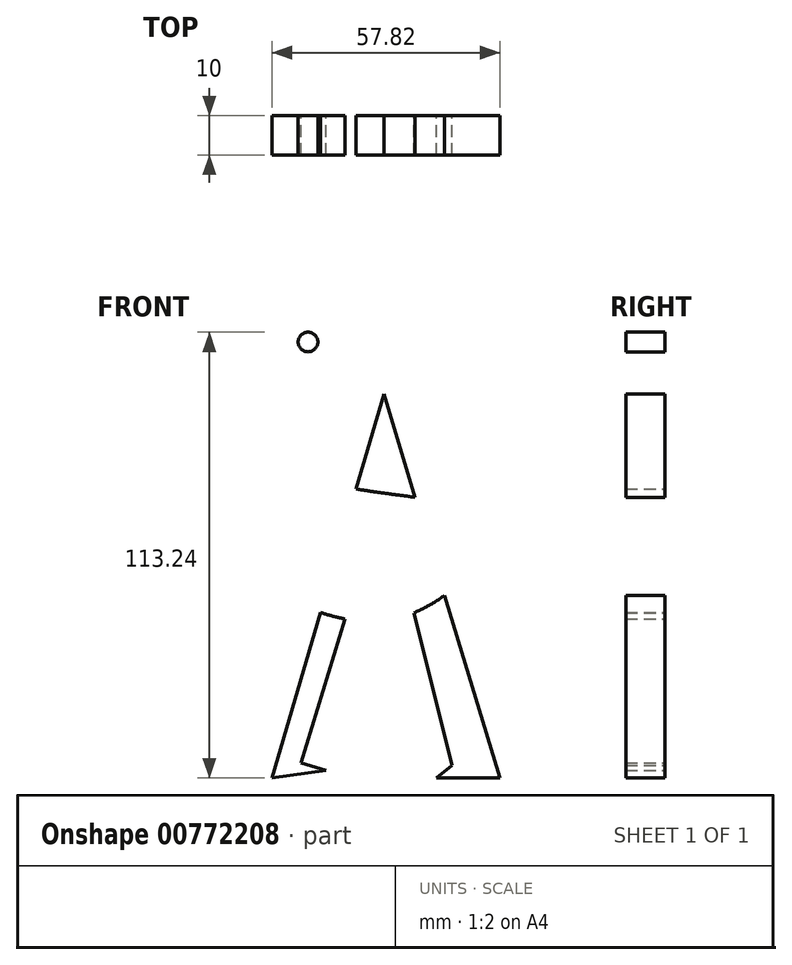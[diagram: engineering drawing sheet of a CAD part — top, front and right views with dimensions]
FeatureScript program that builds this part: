
annotation { "Feature Type Name" : "Feature", "Feature Type Description" : "" }
export const myFeature = defineFeature(function(context is Context, id is Id, definition is map)
    precondition{}
    {
        {
            var Q0;
            Q0=qCreatedBy(makeId("Front.planeOp"),FACE);
            var sketch = newSketch(context, id + "F0", { "sketchPlane" : qUnion([Q0])});
            skFitSpline(sketch, "E0", {"points": [v(-50.96, 0) * mm, v(-14.75, -8.03) * mm, v(8.61, 16.8) * mm, v(-43.07, 32.27) * mm, v(-33.43, 59.72) * mm, v(13.58, 53.58) * mm, v(14.45, 63.51) * mm, v(22.63, 63.51) * mm, v(21.17, 67.6) * mm, v(2.48, 67.02) * mm, v(5.7, 63.8) * mm, v(10.37, 64.1) * mm, v(9.5, 60) * mm, v(-29.35, 67.3) * mm, v(-57.38, 46.28) * mm, v(-41.9, 19.71) * mm, v(-8.03, 16.2) * mm, v(-3.07, 7.15) * mm, v(-24.67, 0) * mm, v(-50.96, 5.4) * mm, v(-63.22, 0) * mm, v(-57.96, -8.61) * mm, v(-61.18, -8.9) * mm, v(-58.55, -12.12) * mm, v(-51.83, -10.37) * mm, v(-53.88, -6.86) * mm, v(-54.75, -6.86) * mm, v(-57.38, -2.2) * mm, v(-50.96, 0) * mm]});
            skLineSegment(sketch, "E1", {"start": v(-45.7, -48.33) * mm, "end": v(-33.5, -6.29) * mm});
            skLineSegment(sketch, "E2", {"start": v(-17.37, 49.2) * mm, "end": v(-9.44, 22.95) * mm});
            skLineSegment(sketch, "E3", {"start": v(12.12, -48.33) * mm, "end": v(-3.94, -48.33) * mm});
            skLineSegment(sketch, "E4", {"start": v(-3.94, -48.33) * mm, "end": v(0, -45.12) * mm});
            skLineSegment(sketch, "E5", {"start": v(0, -45.12) * mm, "end": v(-9.71, -6.4) * mm});
            skLineSegment(sketch, "E6", {"start": v(-17.34, 24) * mm, "end": v(-24.72, 0) * mm});
            skLineSegment(sketch, "E7", {"start": v(-38.4, -44.53) * mm, "end": v(-32.08, -46.47) * mm});
            skLineSegment(sketch, "E8", {"start": v(-32.08, -46.47) * mm, "end": v(-45.7, -48.33) * mm});
            skLineSegment(sketch, "E9.trimOffspring", {"start": v(-27.17, -7.99) * mm, "end": v(-38.4, -44.53) * mm});
            skLineSegment(sketch, "E10.trimOffspring", {"start": v(-11.7, 1.5) * mm, "end": v(-17.34, 24) * mm});
            skLineSegment(sketch, "E11.trimOffspring", {"start": v(-24.38, 25.07) * mm, "end": v(-17.37, 49.2) * mm});
            skLineSegment(sketch, "E12.trimOffspring", {"start": v(-7.3, 15.87) * mm, "end": v(-4.18, 5.57) * mm});
            skLineSegment(sketch, "E13.trimOffspring", {"start": v(-1.9, -1.97) * mm, "end": v(12.12, -48.33) * mm});
            skLineSegment(sketch, "E14.trimOffspring", {"start": v(-31.38, 0.97) * mm, "end": v(-26.58, 17.52) * mm});
            skSolve(sketch);
        }
        {
            var Q0;
            {var subQ0=sQuery(id+"F0.wireOp",EDGE,"E2");Q0=makeQuery(id+"F0.imprint","IMPRINT",FACE,{"disambiguationData":[TD([[makeQuery(id+"F0.imprint","IMPRINT",EDGE,{"derivedFrom":subQ0}),-1.0]])]});}
            var Q1;
            {var subQ0=sQuery(id+"F0.wireOp",EDGE,"E1");Q1=makeQuery(id+"F0.imprint","IMPRINT",FACE,{"disambiguationData":[TD([[makeQuery(id+"F0.imprint","IMPRINT",EDGE,{"derivedFrom":subQ0}),-1.0]])]});}
            var Q2;
            Q2=makeQuery(id+"F0.imprint","IMPRINT",FACE,{"disambiguationData":[TD([[makeQuery(id+"F0.imprint","IMPRINT",EDGE,{"derivedFrom":sQuery(id+"F0.wireOp",EDGE,"E3")}),-1.0]])]});
            extrude(context, id + "F1", {"entities" : qUnion([Q0, Q1, Q2]), "depth" : 10 * mm, "offsetDistance" : 25 * mm});
        }
        {
            var Q0;
            Q0=makeQuery(id+"F1.opExtrude","CAP_FACE",FACE,{"disambiguationData":[OSD([sQuery(id+"F0.wireOp",EDGE,"E0"),sQuery(id+"F0.wireOp",EDGE,"E1"),sQuery(id+"F0.wireOp",EDGE,"E2"),sQuery(id+"F0.wireOp",EDGE,"E3"),sQuery(id+"F0.wireOp",EDGE,"E4"),sQuery(id+"F0.wireOp",EDGE,"E5"),sQuery(id+"F0.wireOp",EDGE,"E6"),sQuery(id+"F0.wireOp",EDGE,"E7"),sQuery(id+"F0.wireOp",EDGE,"E8"),sQuery(id+"F0.wireOp",EDGE,"E9.trimOffspring"),sQuery(id+"F0.wireOp",EDGE,"E10.trimOffspring"),sQuery(id+"F0.wireOp",EDGE,"E0"),sQuery(id+"F0.wireOp",EDGE,"E0"),sQuery(id+"F0.wireOp",EDGE,"E0"),sQuery(id+"F0.wireOp",EDGE,"E11.trimOffspring"),sQuery(id+"F0.wireOp",EDGE,"E12.trimOffspring"),sQuery(id+"F0.wireOp",EDGE,"E13.trimOffspring"),sQuery(id+"F0.wireOp",EDGE,"E14.trimOffspring")])],"isStart":false});
            var sketch = newSketch(context, id + "F2", { "sketchPlane" : qUnion([Q0])});
            skCircle(sketch, "E15", {"center": v(-36.62, 62.41) * mm, "radius": 2.5 * mm});
            skSolve(sketch);
        }
        {
            var Q0;
            Q0=makeQuery(id+"F2.imprint","IMPRINT",FACE,{"disambiguationData":[TD([[makeQuery(id+"F2.imprint","IMPRINT",EDGE,{"derivedFrom":sQuery(id+"F2.wireOp",EDGE,"E15")}),1.0]])]});
            extrude(context, id + "F3", {"entities" : qUnion([Q0]), "operationType" : NewBodyOperationType.ADD, "oppositeDirection" : true, "depth" : 10 * mm, "offsetDistance" : 25 * mm});
        }
    });
